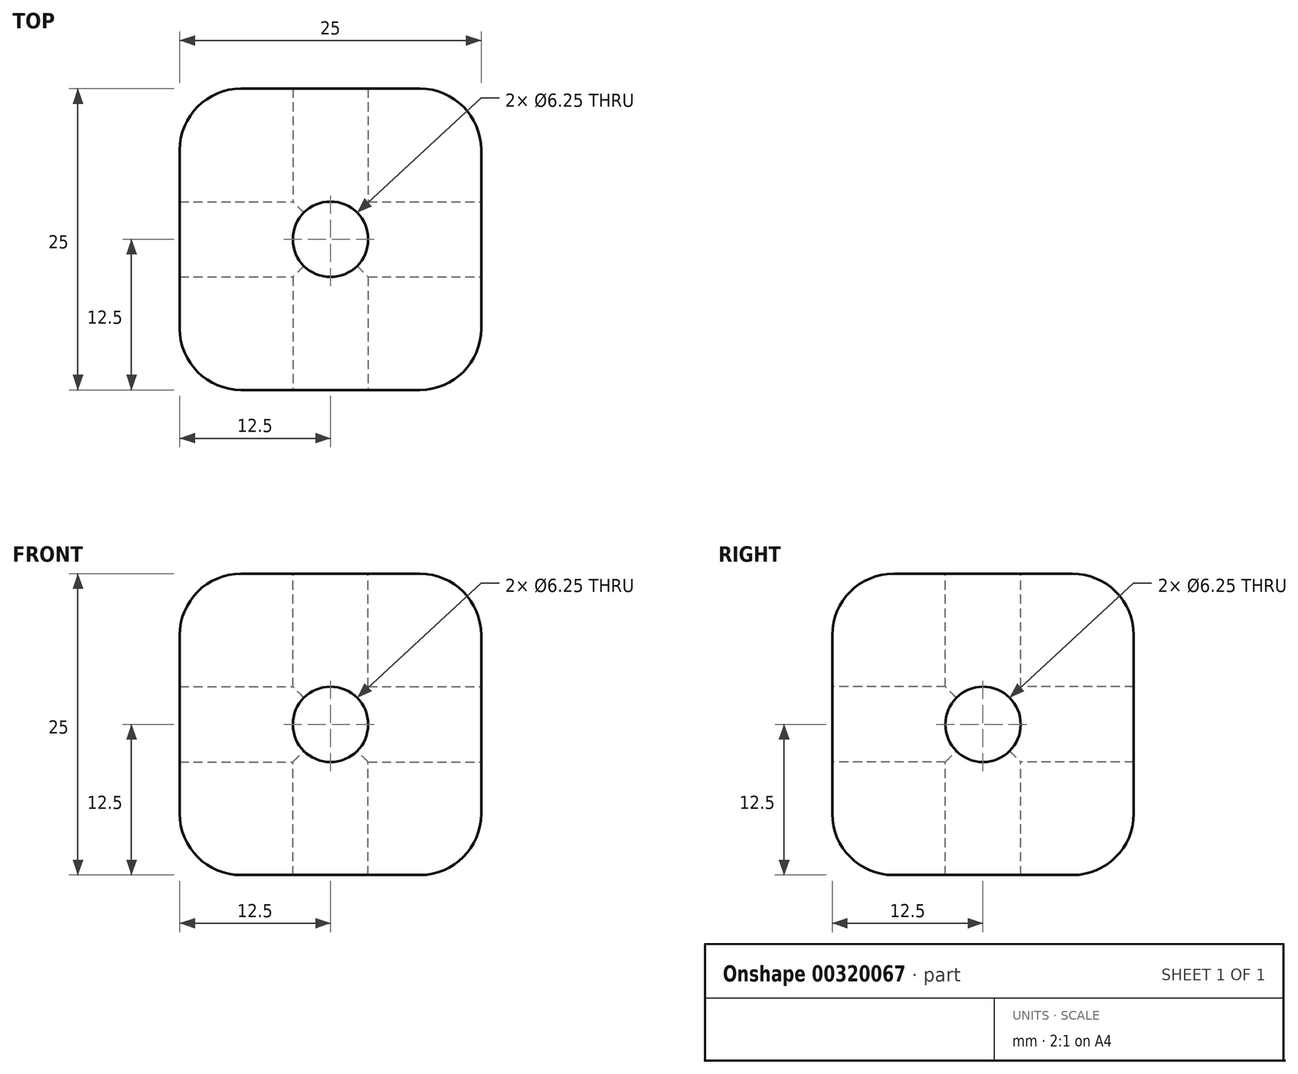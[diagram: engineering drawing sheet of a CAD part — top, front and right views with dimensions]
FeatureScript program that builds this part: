
annotation { "Feature Type Name" : "Feature", "Feature Type Description" : "" }
export const myFeature = defineFeature(function(context is Context, id is Id, definition is map)
    precondition{}
    {
        {
            var Q0;
            Q0=qCreatedBy(makeId("Top.planeOp"),FACE);
            var sketch = newSketch(context, id + "F0", { "sketchPlane" : qUnion([Q0])});
            skLineSegment(sketch, "E0.bottom", {"start": v(0, 0) * mm, "end": v(25, 0) * mm});
            skLineSegment(sketch, "E0.top", {"start": v(0, -25) * mm, "end": v(25, -25) * mm});
            skLineSegment(sketch, "E0.left", {"start": v(0, 0) * mm, "end": v(0, -25) * mm});
            skLineSegment(sketch, "E0.right", {"start": v(25, 0) * mm, "end": v(25, -25) * mm});
            skSolve(sketch);
        }
        {
            var Q0;
            Q0=makeQuery(id+"F0.imprint","IMPRINT",FACE,{"disambiguationData":[TD([[makeQuery(id+"F0.imprint","IMPRINT",EDGE,{"derivedFrom":sQuery(id+"F0.wireOp",EDGE,"E0.bottom")}),-1.0]])]});
            extrude(context, id + "F1", {"entities" : qUnion([Q0]), "depth" : 25 * mm});
        }
        {
            var Q0;
            Q0=makeQuery(id+"F1.opExtrude","SWEPT_FACE",FACE,{"disambiguationData":[OSD([sQuery(id+"F0.wireOp",EDGE,"E0.top")])]});
            var sketch = newSketch(context, id + "F2", { "sketchPlane" : qUnion([Q0])});
            skCircle(sketch, "E1", {"center": v(12.5, 12.5) * mm, "radius": 3.12 * mm});
            skSolve(sketch);
        }
        {
            var Q0;
            Q0=makeQuery(id+"F2.imprint","IMPRINT",FACE,{"disambiguationData":[TD([[makeQuery(id+"F2.imprint","IMPRINT",EDGE,{"derivedFrom":sQuery(id+"F2.wireOp",EDGE,"E1")}),1.0]])]});
            extrude(context, id + "F3", {"entities" : qUnion([Q0]), "operationType" : NewBodyOperationType.REMOVE, "oppositeDirection" : true, "depth" : 25.4 * mm});
        }
        {
            var Q0;
            Q0=makeQuery(id+"F1.opExtrude","SWEPT_FACE",FACE,{"disambiguationData":[OSD([sQuery(id+"F0.wireOp",EDGE,"E0.right")])]});
            var sketch = newSketch(context, id + "F4", { "sketchPlane" : qUnion([Q0])});
            skCircle(sketch, "E2", {"center": v(-12.5, 12.5) * mm, "radius": 3.12 * mm});
            skSolve(sketch);
        }
        {
            var Q0;
            Q0=makeQuery(id+"F4.imprint","IMPRINT",FACE,{"disambiguationData":[TD([[makeQuery(id+"F4.imprint","IMPRINT",EDGE,{"derivedFrom":sQuery(id+"F4.wireOp",EDGE,"E2")}),1.0]])]});
            extrude(context, id + "F5", {"entities" : qUnion([Q0]), "operationType" : NewBodyOperationType.REMOVE, "oppositeDirection" : true, "depth" : 25.4 * mm});
        }
        {
            var Q0;
            Q0=makeQuery(id+"F1.opExtrude","CAP_FACE",FACE,{"disambiguationData":[OSD([sQuery(id+"F0.wireOp",EDGE,"E0.bottom"),sQuery(id+"F0.wireOp",EDGE,"E0.top"),sQuery(id+"F0.wireOp",EDGE,"E0.left"),sQuery(id+"F0.wireOp",EDGE,"E0.right")])],"isStart":false});
            var sketch = newSketch(context, id + "F6", { "sketchPlane" : qUnion([Q0])});
            skCircle(sketch, "E3", {"center": v(12.5, -12.5) * mm, "radius": 3.12 * mm});
            skPoint(sketch, "E3.centerSnap0", {"position": v(25, -12.5) * mm});
            skPoint(sketch, "E3.centerSnap1", {"position": v(12.5, -25) * mm});
            skSolve(sketch);
        }
        {
            var Q0;
            Q0=makeQuery(id+"F6.imprint","IMPRINT",FACE,{"disambiguationData":[TD([[makeQuery(id+"F6.imprint","IMPRINT",EDGE,{"derivedFrom":sQuery(id+"F6.wireOp",EDGE,"E3")}),1.0]])]});
            extrude(context, id + "F7", {"entities" : qUnion([Q0]), "operationType" : NewBodyOperationType.REMOVE, "oppositeDirection" : true, "depth" : 25.4 * mm});
        }
        {
            var Q0;
            Q0=makeQuery(id+"F1.opExtrude","CAP_EDGE",EDGE,{"disambiguationData":[OSD([sQuery(id+"F0.wireOp",EDGE,"E0.top")])],"isStart":true});
            fillet(context, id + "F8", {"entities" : qUnion([Q0]), "radius" : 5.08 * mm, "tangentPropagation" : true, "allowEdgeOverflow" : false});
        }
        {
            var Q0;
            Q0=makeQuery(id+"F1.opExtrude","CAP_EDGE",EDGE,{"disambiguationData":[OSD([sQuery(id+"F0.wireOp",EDGE,"E0.bottom")])],"isStart":true});
            fillet(context, id + "F9", {"entities" : qUnion([Q0]), "radius" : 5.08 * mm, "tangentPropagation" : true, "allowEdgeOverflow" : false});
        }
        {
            var Q0;
            Q0=makeQuery(id+"F1.opExtrude","CAP_EDGE",EDGE,{"disambiguationData":[OSD([sQuery(id+"F0.wireOp",EDGE,"E0.bottom")])],"isStart":false});
            fillet(context, id + "F10", {"entities" : qUnion([Q0]), "radius" : 5.08 * mm, "tangentPropagation" : true, "allowEdgeOverflow" : false});
        }
        {
            var Q0;
            Q0=makeQuery(id+"F1.opExtrude","CAP_EDGE",EDGE,{"disambiguationData":[OSD([sQuery(id+"F0.wireOp",EDGE,"E0.top")])],"isStart":false});
            fillet(context, id + "F11", {"entities" : qUnion([Q0]), "radius" : 5.08 * mm, "tangentPropagation" : true, "allowEdgeOverflow" : false});
        }
        {
            var Q0;
            Q0=makeQuery(id+"F1.opExtrude","SWEPT_EDGE",EDGE,{"disambiguationData":[OSD([sQuery(id+"F0.wireOp",EDGE,"E0.bottom"),sQuery(id+"F0.wireOp",EDGE,"E0.right")])]});
            fillet(context, id + "F12", {"entities" : qUnion([Q0]), "radius" : 5.08 * mm, "tangentPropagation" : true, "allowEdgeOverflow" : false});
        }
        {
            var Q0;
            Q0=makeQuery(id+"F1.opExtrude","CAP_EDGE",EDGE,{"disambiguationData":[OSD([sQuery(id+"F0.wireOp",EDGE,"E0.left")])],"isStart":false});
            fillet(context, id + "F13", {"entities" : qUnion([Q0]), "radius" : 5.08 * mm, "tangentPropagation" : true, "allowEdgeOverflow" : false});
        }
    });
